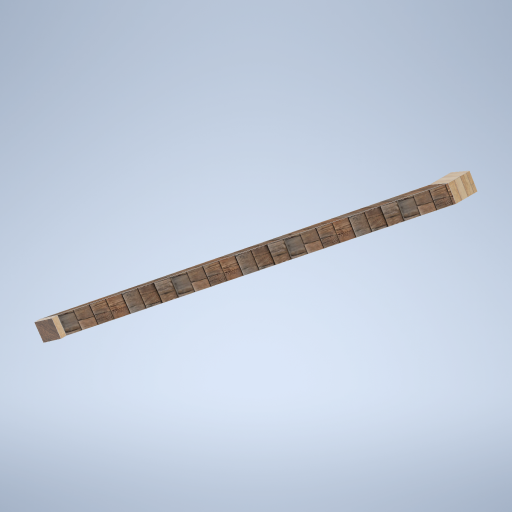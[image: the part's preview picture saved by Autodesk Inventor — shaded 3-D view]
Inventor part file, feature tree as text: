
AUTODESK INVENTOR PART (.ipt)
format: ipt  version: 2024.2 (Build 282272000, 272)  size: 317,952 bytes
history: native  units: mm
features: sketch x4, plane x2, extrude x2, loft x1, projected_geometry x1
ambient origin geometry x8: Origin, YZ Plane, XZ Plane, XY Plane, X Axis, Y Axis, Z Axis, Center Point
bodies: Solid1 (feature_tree)
feature tree (10):
  sketch  "Sketch5"  dims[d10=0.0mm d11=3749.0mm d12=0.0mm d13=90.0deg]
  plane  "Work Plane6"
  loft  "Loft1"
  extrude  "Extrusion1"  Depth=200.0mm TaperAngle=0.0deg
  extrude  "Extrusion2"  [1 undecoded]
  plane  "Work Plane5"
  sketch  "Sketch6"  dims[d14=0.0mm d15=90.0deg d16=200.0mm d17=0.0mm]
  sketch  "Sketch7"  dims[d18=50.0mm d19=0.0mm]
  sketch  "Sketch8"
  projected_geometry  "Projected Loop1"
note: 1 required parameter value undecoded (feature->parameter linkage not recoverable at this tier; creation-order binding heuristic only, values carry confidence <= 0.55)
